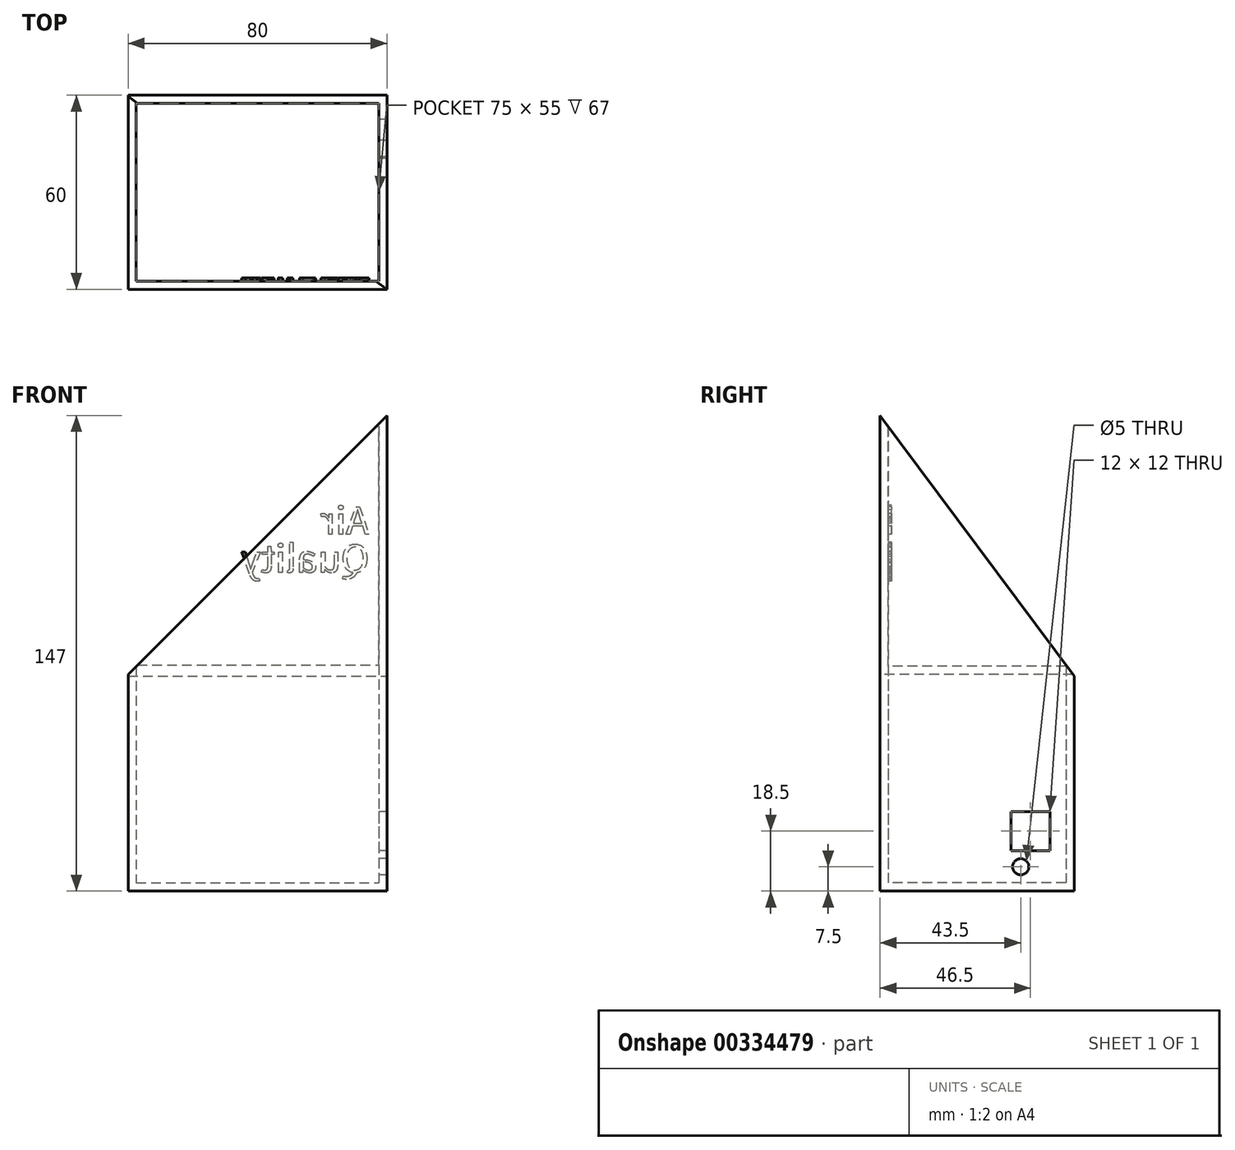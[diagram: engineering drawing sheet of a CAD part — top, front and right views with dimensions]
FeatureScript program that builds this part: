
annotation { "Feature Type Name" : "Feature", "Feature Type Description" : "" }
export const myFeature = defineFeature(function(context is Context, id is Id, definition is map)
    precondition{}
    {
        {
            var Q0;
            Q0=qCreatedBy(makeId("Top.planeOp"),FACE);
            var sketch = newSketch(context, id + "F0", { "sketchPlane" : qUnion([Q0])});
            skLineSegment(sketch, "E0.bottom", {"start": v(-40, 30) * mm, "end": v(40, 30) * mm});
            skLineSegment(sketch, "E0.top", {"start": v(-40, -30) * mm, "end": v(40, -30) * mm});
            skLineSegment(sketch, "E0.left", {"start": v(-40, 30) * mm, "end": v(-40, -30) * mm});
            skLineSegment(sketch, "E0.right", {"start": v(40, 30) * mm, "end": v(40, -30) * mm});
            skPoint(sketch, "E0.middle", {"position": v(0, 0) * mm});
            skSolve(sketch);
        }
        {
            var Q0;
            Q0=makeQuery(id+"F0.imprint","IMPRINT",FACE,{"disambiguationData":[TD([[makeQuery(id+"F0.imprint","IMPRINT",EDGE,{"derivedFrom":sQuery(id+"F0.wireOp",EDGE,"E0.bottom")}),-1.0]])]});
            extrude(context, id + "F1", {"entities" : qUnion([Q0]), "depth" : 2 * mm});
        }
        {
            var Q0;
            Q0=makeQuery(id+"F1.opExtrude","CAP_FACE",FACE,{"disambiguationData":[OSD([sQuery(id+"F0.wireOp",EDGE,"E0.bottom"),sQuery(id+"F0.wireOp",EDGE,"E0.top"),sQuery(id+"F0.wireOp",EDGE,"E0.left"),sQuery(id+"F0.wireOp",EDGE,"E0.right")])],"isStart":false});
            extrude(context, id + "F2", {"entities" : qUnion([Q0]), "operationType" : NewBodyOperationType.ADD, "depth" : 145 * mm});
        }
        {
            var Q0;
            Q0=makeQuery(id+"F2.opExtrude","CAP_FACE",FACE,{"disambiguationData":[OSD([sQuery(id+"F0.wireOp",EDGE,"E0.bottom"),sQuery(id+"F0.wireOp",EDGE,"E0.top"),sQuery(id+"F0.wireOp",EDGE,"E0.left"),sQuery(id+"F0.wireOp",EDGE,"E0.right")])],"isStart":false});
            shell(context, id + "F3", {"entities" : qUnion([Q0]), "thickness" : 2.5 * mm});
        }
        {
            var Q0;
            {var subQ0=sQuery(id+"F0.wireOp",EDGE,"E0.top");Q0=makeQuery(id+"F2.boolean.opBoolean","MERGE",FACE,{"derivedFrom":[makeQuery(id+"F1.opExtrude","SWEPT_FACE",FACE,{"disambiguationData":[OSD([subQ0])]}),makeQuery(id+"F2.opExtrude","SWEPT_FACE",FACE,{"disambiguationData":[OSD([subQ0])]})]});}
            var sketch = newSketch(context, id + "F4", { "sketchPlane" : qUnion([Q0])});
            skLineSegment(sketch, "E1", {"start": v(-40, 147) * mm, "end": v(40, 147) * mm});
            skLineSegment(sketch, "E2", {"start": v(40, 147) * mm, "end": v(-40, 67) * mm});
            skLineSegment(sketch, "E3", {"start": v(-40, 67) * mm, "end": v(-40, 147) * mm});
            skSolve(sketch);
        }
        {
            var Q0;
            Q0=makeQuery(id+"F4.imprint","IMPRINT",FACE,{"disambiguationData":[TD([[makeQuery(id+"F4.imprint","IMPRINT",EDGE,{"derivedFrom":sQuery(id+"F4.wireOp",EDGE,"E1")}),-1.0]])]});
            extrude(context, id + "F5", {"entities" : qUnion([Q0]), "operationType" : NewBodyOperationType.REMOVE, "oppositeDirection" : true, "depth" : 60 * mm});
        }
        {
            var Q0;
            {var subQ0=sQuery(id+"F0.wireOp",EDGE,"E0.right");Q0=makeQuery(id+"F2.boolean.opBoolean","MERGE",FACE,{"derivedFrom":[makeQuery(id+"F1.opExtrude","SWEPT_FACE",FACE,{"disambiguationData":[OSD([subQ0])]}),makeQuery(id+"F2.opExtrude","SWEPT_FACE",FACE,{"disambiguationData":[OSD([subQ0])]})]});}
            var sketch = newSketch(context, id + "F6", { "sketchPlane" : qUnion([Q0])});
            skLineSegment(sketch, "E4", {"start": v(30, 147) * mm, "end": v(30, 66.5) * mm});
            skLineSegment(sketch, "E5", {"start": v(30, 66.5) * mm, "end": v(-30, 147) * mm});
            skLineSegment(sketch, "E6", {"start": v(-30, 147) * mm, "end": v(30, 147) * mm});
            skSolve(sketch);
        }
        {
            var Q0;
            Q0=makeQuery(id+"F6.imprint","IMPRINT",FACE,{"disambiguationData":[TD([[makeQuery(id+"F6.imprint","IMPRINT",EDGE,{"derivedFrom":sQuery(id+"F6.wireOp",EDGE,"E4")}),-1.0]])]});
            extrude(context, id + "F7", {"entities" : qUnion([Q0]), "operationType" : NewBodyOperationType.REMOVE, "oppositeDirection" : true, "depth" : 80 * mm});
        }
        {
            var Q0;
            Q0=makeQuery(id+"F3.opShell","OFFSET_FACE",FACE,{"disambiguationData":[OSD([sQuery(id+"F0.wireOp",EDGE,"E0.right")])]});
            var sketch = newSketch(context, id + "F8", { "sketchPlane" : qUnion([Q0])});
            skLineSegment(sketch, "E7.bottom", {"start": v(-10.5, 24.5) * mm, "end": v(-22.5, 24.5) * mm});
            skLineSegment(sketch, "E7.top", {"start": v(-10.5, 12.5) * mm, "end": v(-22.5, 12.5) * mm});
            skLineSegment(sketch, "E7.left", {"start": v(-10.5, 24.5) * mm, "end": v(-10.5, 12.5) * mm});
            skLineSegment(sketch, "E7.right", {"start": v(-22.5, 24.5) * mm, "end": v(-22.5, 12.5) * mm});
            skPoint(sketch, "E7.middle", {"position": v(-16.5, 18.5) * mm});
            skCircle(sketch, "E8", {"center": v(-13.5, 7.5) * mm, "radius": 2.5 * mm});
            skSolve(sketch);
        }
        {
            var Q0;
            Q0=makeQuery(id+"F8.imprint","IMPRINT",FACE,{"disambiguationData":[TD([[makeQuery(id+"F8.imprint","IMPRINT",EDGE,{"derivedFrom":sQuery(id+"F8.wireOp",EDGE,"E7.bottom")}),1.0]])]});
            var Q1;
            Q1=makeQuery(id+"F8.imprint","IMPRINT",FACE,{"disambiguationData":[TD([[makeQuery(id+"F8.imprint","IMPRINT",EDGE,{"derivedFrom":sQuery(id+"F8.wireOp",EDGE,"E8")}),1.0]])]});
            extrude(context, id + "F9", {"entities" : qUnion([Q0, Q1]), "operationType" : NewBodyOperationType.REMOVE, "oppositeDirection" : true, "depth" : 25 * mm});
        }
        {
            var Q0;
            Q0=makeQuery(id+"F3.opShell","OFFSET_FACE",FACE,{"disambiguationData":[OSD([sQuery(id+"F0.wireOp",EDGE,"E0.top")])]});
            var sketch = newSketch(context, id + "F10", { "sketchPlane" : qUnion([Q0])});
            skText(sketch, "E9", { "text": "Air \nQuality\n", "fontName": "NotoSansCJKjp-Regular.otf"});
            const initialGuessF10  = {"E9": [-0.0345, 0.11021, 1, 0, 0.00844]};
            skSetInitialGuess(sketch, initialGuessF10);
            skSolve(sketch);
        }
        {
            var Q0;
            Q0 = qSketchRegion(id + "F10", true);
            extrude(context, id + "F11", {"entities" : qUnion([Q0]), "operationType" : NewBodyOperationType.ADD, "depth" : 1 * mm});
        }
    });
